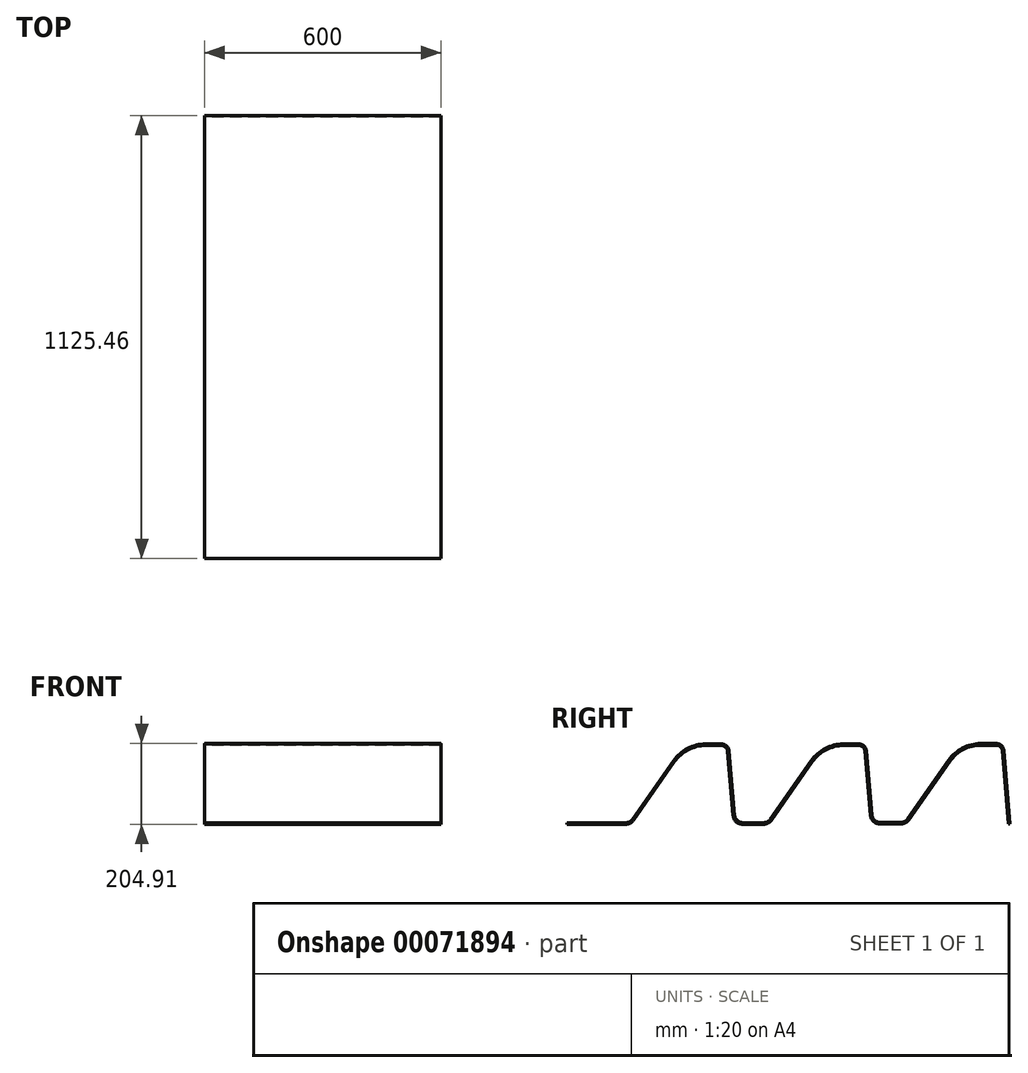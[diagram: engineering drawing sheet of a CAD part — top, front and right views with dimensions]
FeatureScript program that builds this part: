
annotation { "Feature Type Name" : "Feature", "Feature Type Description" : "" }
export const myFeature = defineFeature(function(context is Context, id is Id, definition is map)
    precondition{}
    {
        {
            var Q0;
            Q0=qCreatedBy(makeId("Right.planeOp"),FACE);
            var sketch = newSketch(context, id + "F0", { "sketchPlane" : qUnion([Q0])});
            skLineSegment(sketch, "E0", {"start": v(5.97, 8.53) * mm, "end": v(110.18, 157.36) * mm});
            skLineSegment(sketch, "E1", {"start": v(192.1, 200) * mm, "end": v(231.67, 200) * mm});
            skPoint(sketch, "E2.visualSharp", {"position": v(140.04, 200) * mm});
            skArc(sketch, "E2.filletArc", {"start": v(192.1, 200) * mm, "mid": v(145.92, 188.7) * mm, "end": v(110.18, 157.36) * mm});
            skLineSegment(sketch, "E3", {"start": v(251.6, 181.74) * mm, "end": v(265.9, 18.26) * mm});
            skPoint(sketch, "E4.visualSharp", {"position": v(250, 200) * mm});
            skArc(sketch, "E4.filletArc", {"start": v(251.6, 181.74) * mm, "mid": v(245.19, 194.75) * mm, "end": v(231.67, 200) * mm});
            skLineSegment(sketch, "E5.1.0.0", {"start": v(600.6, 182.66) * mm, "end": v(614.9, 19.17) * mm});
            skPoint(sketch, "E5.1.0.1", {"position": v(600, 200) * mm});
            skArc(sketch, "E5.1.0.2", {"start": v(542.1, 200) * mm, "mid": v(495.92, 188.7) * mm, "end": v(460.18, 157.36) * mm});
            skPoint(sketch, "E5.1.0.3", {"position": v(490.04, 200) * mm});
            skLineSegment(sketch, "E5.1.0.5", {"start": v(542.1, 200) * mm, "end": v(581.67, 200) * mm});
            skLineSegment(sketch, "E5.1.0.6", {"start": v(355.97, 8.53) * mm, "end": v(460.18, 157.36) * mm});
            skArc(sketch, "E5.1.0.7", {"start": v(600.6, 182.66) * mm, "mid": v(594.5, 195) * mm, "end": v(581.67, 200) * mm});
            skLineSegment(sketch, "E5.2.0.0", {"start": v(949.6, 183.56) * mm, "end": v(965.05, -3.09) * mm});
            skPoint(sketch, "E5.2.0.1", {"position": v(950, 200) * mm});
            skArc(sketch, "E5.2.0.2", {"start": v(891.1, 200.91) * mm, "mid": v(844.93, 189.61) * mm, "end": v(809.19, 158.27) * mm});
            skPoint(sketch, "E5.2.0.3", {"position": v(840.04, 200) * mm});
            skLineSegment(sketch, "E5.2.0.5", {"start": v(891.1, 200.91) * mm, "end": v(930.68, 200.91) * mm});
            skLineSegment(sketch, "E5.2.0.6", {"start": v(704.98, 9.44) * mm, "end": v(809.19, 158.27) * mm});
            skArc(sketch, "E5.2.0.7", {"start": v(949.6, 183.56) * mm, "mid": v(943.52, 195.92) * mm, "end": v(930.68, 200.91) * mm});
            skLineSegment(sketch, "E6", {"start": v(634.83, 0.91) * mm, "end": v(688.6, 0.91) * mm});
            skLineSegment(sketch, "E7", {"start": v(285.82, 0) * mm, "end": v(339.59, 0) * mm});
            skLineSegment(sketch, "E8", {"start": v(-10.41, 0) * mm, "end": v(-160.4, 0) * mm});
            skPoint(sketch, "E9.visualSharp", {"position": v(267.5, 0) * mm});
            skArc(sketch, "E9.filletArc", {"start": v(265.9, 18.26) * mm, "mid": v(272.31, 5.25) * mm, "end": v(285.82, 0) * mm});
            skPoint(sketch, "E10.visualSharp", {"position": v(350, 0) * mm});
            skArc(sketch, "E10.filletArc", {"start": v(339.59, 0) * mm, "mid": v(348.82, 2.26) * mm, "end": v(355.97, 8.53) * mm});
            skPoint(sketch, "E11.visualSharp", {"position": v(616.5, 0.91) * mm});
            skArc(sketch, "E11.filletArc", {"start": v(614.9, 19.17) * mm, "mid": v(621.32, 6.17) * mm, "end": v(634.83, 0.91) * mm});
            skPoint(sketch, "E12.visualSharp", {"position": v(699, 0.91) * mm});
            skArc(sketch, "E12.filletArc", {"start": v(688.6, 0.91) * mm, "mid": v(697.83, 3.17) * mm, "end": v(704.98, 9.44) * mm});
            skPoint(sketch, "E13.visualSharp", {"position": v(0, 0) * mm});
            skArc(sketch, "E13.filletArc", {"start": v(-10.41, 0) * mm, "mid": v(-1.18, 2.26) * mm, "end": v(5.97, 8.53) * mm});
            skLineSegment(sketch, "E14.16", {"start": v(945.62, 183.22) * mm, "end": v(961.03, -3.09) * mm});
            skArc(sketch, "E14.17", {"start": v(339.59, -4) * mm, "mid": v(350.67, -1.29) * mm, "end": v(359.25, 6.23) * mm});
            skLineSegment(sketch, "E14.18", {"start": v(285.82, -4) * mm, "end": v(339.59, -4) * mm});
            skArc(sketch, "E14.19", {"start": v(261.92, 17.9) * mm, "mid": v(269.61, 2.3) * mm, "end": v(285.82, -4) * mm});
            skLineSegment(sketch, "E14.20", {"start": v(247.61, 181.4) * mm, "end": v(261.92, 17.9) * mm});
            skArc(sketch, "E14.21", {"start": v(247.61, 181.4) * mm, "mid": v(242.48, 191.8) * mm, "end": v(231.67, 196) * mm});
            skLineSegment(sketch, "E14.22", {"start": v(192.1, 196) * mm, "end": v(231.67, 196) * mm});
            skLineSegment(sketch, "E14.23", {"start": v(-10.41, -4) * mm, "end": v(-160.41, -4) * mm});
            skArc(sketch, "E14.24", {"start": v(-10.41, -4) * mm, "mid": v(0.67, -1.29) * mm, "end": v(9.25, 6.23) * mm});
            skLineSegment(sketch, "E14.25", {"start": v(9.25, 6.23) * mm, "end": v(113.46, 155.06) * mm});
            skArc(sketch, "E14.26", {"start": v(192.1, 196) * mm, "mid": v(147.77, 185.15) * mm, "end": v(113.46, 155.06) * mm});
            skLineSegment(sketch, "E14.27", {"start": v(359.25, 6.23) * mm, "end": v(463.46, 155.06) * mm});
            skArc(sketch, "E14.28", {"start": v(542.1, 196) * mm, "mid": v(497.77, 185.15) * mm, "end": v(463.46, 155.06) * mm});
            skLineSegment(sketch, "E14.29", {"start": v(542.1, 196) * mm, "end": v(581.67, 196) * mm});
            skArc(sketch, "E14.30", {"start": v(596.62, 182.3) * mm, "mid": v(591.8, 192.06) * mm, "end": v(581.67, 196) * mm});
            skLineSegment(sketch, "E14.31", {"start": v(596.62, 182.3) * mm, "end": v(610.92, 18.82) * mm});
            skArc(sketch, "E14.32", {"start": v(610.92, 18.82) * mm, "mid": v(618.61, 3.22) * mm, "end": v(634.83, -3.09) * mm});
            skLineSegment(sketch, "E14.33", {"start": v(634.83, -3.09) * mm, "end": v(688.6, -3.09) * mm});
            skArc(sketch, "E14.34", {"start": v(688.6, -3.09) * mm, "mid": v(699.67, -0.38) * mm, "end": v(708.25, 7.15) * mm});
            skLineSegment(sketch, "E14.35", {"start": v(708.25, 7.15) * mm, "end": v(812.46, 155.98) * mm});
            skArc(sketch, "E14.36", {"start": v(891.1, 196.91) * mm, "mid": v(846.77, 186.07) * mm, "end": v(812.46, 155.98) * mm});
            skLineSegment(sketch, "E14.37", {"start": v(891.1, 196.91) * mm, "end": v(930.68, 196.91) * mm});
            skArc(sketch, "E14.38", {"start": v(945.62, 183.22) * mm, "mid": v(940.81, 192.97) * mm, "end": v(930.68, 196.91) * mm});
            skLineSegment(sketch, "E15", {"start": v(-160.4, 0) * mm, "end": v(-160.41, -4) * mm});
            skLineSegment(sketch, "E16", {"start": v(961.03, -3.09) * mm, "end": v(965.05, -3.09) * mm});
            skSolve(sketch);
        }
        {
            var Q0;
            Q0=qSketchRegion(id+"F0",true);
            extrude(context, id + "F1", {"entities" : qUnion([Q0]), "depth" : 300 * mm, "hasSecondDirection" : true, "secondDirectionOppositeDirection" : true, "secondDirectionDepth" : 300 * mm});
        }
    });
